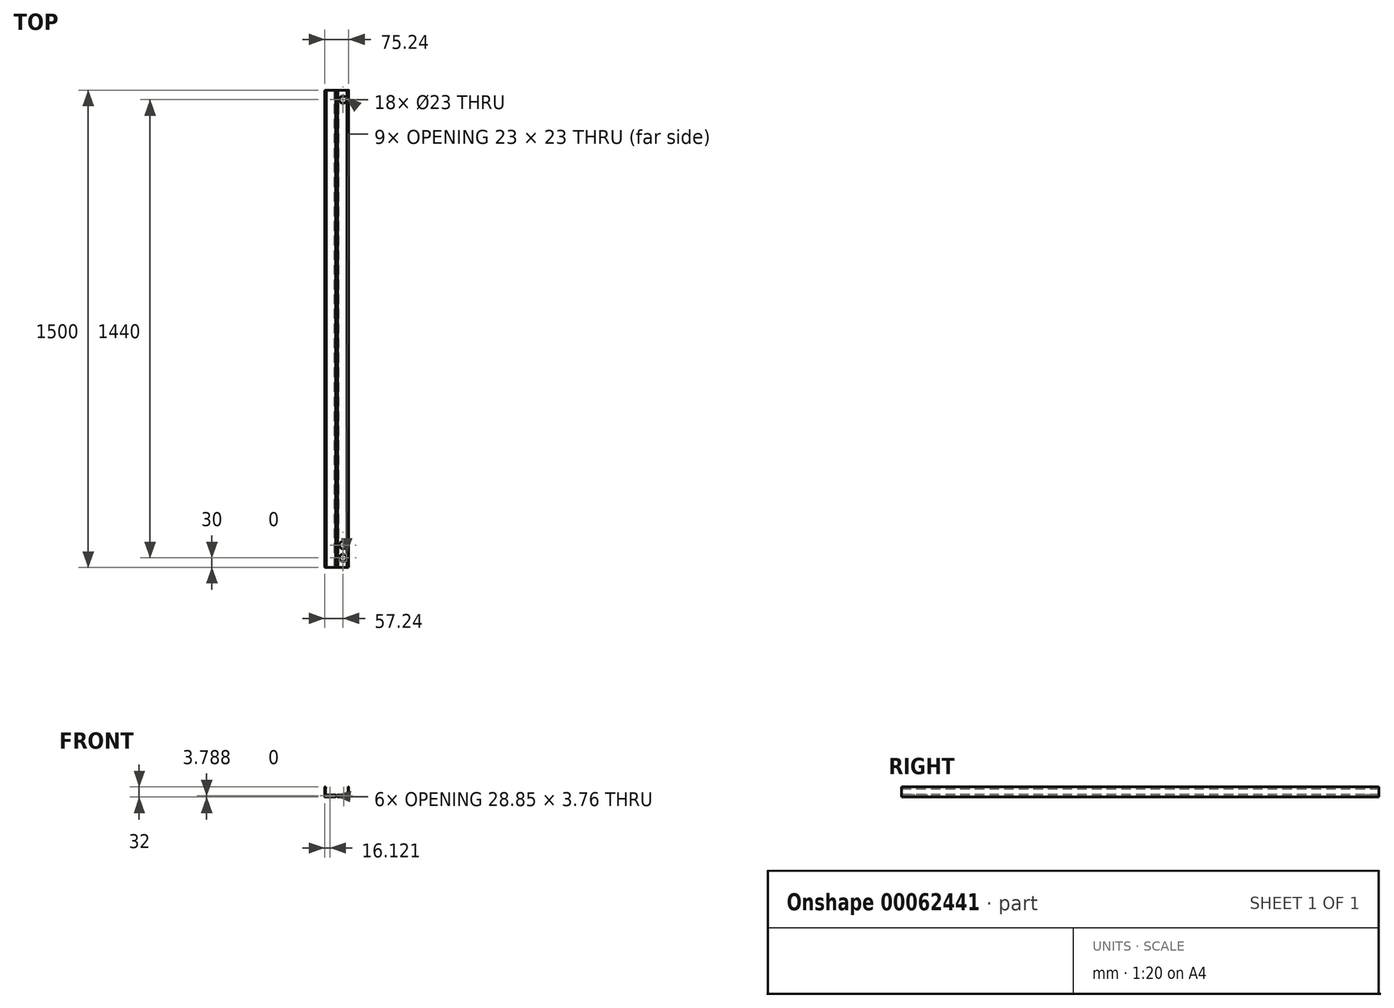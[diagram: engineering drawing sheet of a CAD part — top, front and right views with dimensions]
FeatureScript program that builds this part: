
annotation { "Feature Type Name" : "Feature", "Feature Type Description" : "" }
export const myFeature = defineFeature(function(context is Context, id is Id, definition is map)
    precondition{}
    {
        {
            var Q0;
            Q0=qCreatedBy(makeId("Front.planeOp"),FACE);
            var sketch = newSketch(context, id + "F0", { "sketchPlane" : qUnion([Q0])});
            skLineSegment(sketch, "E0.bottom", {"start": v(0, 0) * mm, "end": v(-34.36, 0) * mm});
            skLineSegment(sketch, "E0.top", {"start": v(0, 32) * mm, "end": v(-2, 32) * mm});
            skLineSegment(sketch, "E0.left", {"start": v(0, 0) * mm, "end": v(0, 32) * mm});
            skLineSegment(sketch, "E0.right", {"start": v(-75.24, 0) * mm, "end": v(-75.24, 32) * mm});
            skLineSegment(sketch, "E1", {"start": v(-73.24, 32) * mm, "end": v(-73.24, 30) * mm});
            skLineSegment(sketch, "E2", {"start": v(-73.24, 30) * mm, "end": v(-71.61, 30) * mm});
            skLineSegment(sketch, "E3", {"start": v(-71.61, 30) * mm, "end": v(-71.5, 28.38) * mm});
            skLineSegment(sketch, "E4", {"start": v(-71.5, 28.38) * mm, "end": v(-73.24, 26.53) * mm});
            skLineSegment(sketch, "E5", {"start": v(-73.24, 26.53) * mm, "end": v(-73.24, 9.03) * mm});
            skLineSegment(sketch, "E6", {"start": v(-73.24, 9.03) * mm, "end": v(-69.92, 7.45) * mm});
            skLineSegment(sketch, "E7", {"start": v(-69.92, 7.45) * mm, "end": v(-41.29, 7.45) * mm});
            skLineSegment(sketch, "E8", {"start": v(-41.29, 7.45) * mm, "end": v(-39.54, 5.37) * mm});
            skLineSegment(sketch, "E9.MirrorCS", {"start": v(-2, 26.4) * mm, "end": v(-2.4, 9.03) * mm});
            skLineSegment(sketch, "E10.MirrorCS", {"start": v(-3.74, 28.26) * mm, "end": v(-2, 26.4) * mm});
            skLineSegment(sketch, "E11.MirrorCS", {"start": v(-2, 32) * mm, "end": v(-2, 30) * mm});
            skLineSegment(sketch, "E12.MirrorCS", {"start": v(-2.4, 9.03) * mm, "end": v(-5.72, 7.45) * mm});
            skLineSegment(sketch, "E13.MirrorCS", {"start": v(-5.72, 7.45) * mm, "end": v(-34.35, 7.45) * mm});
            skLineSegment(sketch, "E14.MirrorCS", {"start": v(-34.35, 7.45) * mm, "end": v(-36.1, 5.37) * mm});
            skLineSegment(sketch, "E15.MirrorCS", {"start": v(-3.63, 30) * mm, "end": v(-3.74, 28.26) * mm});
            skLineSegment(sketch, "E16.MirrorCS", {"start": v(-2, 30) * mm, "end": v(-3.63, 30) * mm});
            skLineSegment(sketch, "E17", {"start": v(-36.1, 5.37) * mm, "end": v(-39.54, 5.37) * mm});
            skLineSegment(sketch, "E18.trimOffspring", {"start": v(-73.24, 32) * mm, "end": v(-75.24, 32) * mm});
            skLineSegment(sketch, "E19", {"start": v(-44.7, 1.91) * mm, "end": v(-73.36, 1.91) * mm});
            skLineSegment(sketch, "E20", {"start": v(-73.36, 1.91) * mm, "end": v(-73.4, 2.5) * mm});
            skLineSegment(sketch, "E21", {"start": v(-73.4, 2.5) * mm, "end": v(-71.75, 2.59) * mm});
            skLineSegment(sketch, "E22", {"start": v(-71.75, 2.59) * mm, "end": v(-71.79, 3.29) * mm});
            skLineSegment(sketch, "E23", {"start": v(-71.79, 3.29) * mm, "end": v(-73.54, 3.64) * mm});
            skLineSegment(sketch, "E24", {"start": v(-73.54, 3.64) * mm, "end": v(-73.2, 5.33) * mm});
            skLineSegment(sketch, "E25", {"start": v(-73.2, 5.33) * mm, "end": v(-71.6, 5.67) * mm});
            skLineSegment(sketch, "E26", {"start": v(-71.6, 5.67) * mm, "end": v(-70.68, 4.5) * mm});
            skLineSegment(sketch, "E27", {"start": v(-70.68, 4.5) * mm, "end": v(-69.94, 5.34) * mm});
            skLineSegment(sketch, "E28", {"start": v(-69.94, 5.34) * mm, "end": v(-44.7, 5.34) * mm});
            skLineSegment(sketch, "E29", {"start": v(-44.7, 5.34) * mm, "end": v(-44.7, 1.91) * mm});
            skLineSegment(sketch, "E30", {"start": v(-37.74, 4.09) * mm, "end": v(-41.06, 4.09) * mm});
            skLineSegment(sketch, "E31", {"start": v(-41.06, 4.09) * mm, "end": v(-42.08, 5.37) * mm});
            skLineSegment(sketch, "E32", {"start": v(-42.08, 5.37) * mm, "end": v(-43.15, 5.34) * mm});
            skLineSegment(sketch, "E33", {"start": v(-43.15, 5.34) * mm, "end": v(-43.04, 1.31) * mm});
            skLineSegment(sketch, "E34", {"start": v(-43.04, 1.31) * mm, "end": v(-41, 1.28) * mm});
            skLineSegment(sketch, "E35", {"start": v(-41, 1.28) * mm, "end": v(-41, 0) * mm});
            skLineSegment(sketch, "E36.trimOffspring", {"start": v(-41, 0) * mm, "end": v(-75.24, 0) * mm});
            skLineSegment(sketch, "E37.MirrorCS", {"start": v(-32.33, 1.31) * mm, "end": v(-34.36, 1.28) * mm});
            skLineSegment(sketch, "E38.MirrorCS", {"start": v(-37.74, 4.09) * mm, "end": v(-34.3, 4.09) * mm});
            skLineSegment(sketch, "E39.MirrorCS", {"start": v(-32.22, 5.34) * mm, "end": v(-32.33, 1.31) * mm});
            skLineSegment(sketch, "E40.MirrorCS", {"start": v(-34.36, 0) * mm, "end": v(-0.12, 0) * mm});
            skLineSegment(sketch, "E41.MirrorCS", {"start": v(-33.29, 5.37) * mm, "end": v(-32.22, 5.34) * mm});
            skLineSegment(sketch, "E42.MirrorCS", {"start": v(-34.36, 1.28) * mm, "end": v(-34.36, 0) * mm});
            skLineSegment(sketch, "E43.MirrorCS", {"start": v(-34.3, 4.09) * mm, "end": v(-33.29, 5.37) * mm});
            skLineSegment(sketch, "E44.MirrorCS", {"start": v(-75.24, 0) * mm, "end": v(-41, 0) * mm});
            skLineSegment(sketch, "E45.MirrorCS", {"start": v(-2.04, 5.33) * mm, "end": v(-3.64, 5.67) * mm});
            skLineSegment(sketch, "E46.MirrorCS", {"start": v(-4.56, 4.5) * mm, "end": v(-5.3, 5.34) * mm});
            skLineSegment(sketch, "E47.MirrorCS", {"start": v(-3.49, 2.59) * mm, "end": v(-3.45, 3.29) * mm});
            skLineSegment(sketch, "E48.MirrorCS", {"start": v(-1.88, 1.91) * mm, "end": v(-1.85, 2.5) * mm});
            skLineSegment(sketch, "E49.MirrorCS", {"start": v(-3.64, 5.67) * mm, "end": v(-4.56, 4.5) * mm});
            skLineSegment(sketch, "E50.MirrorCS", {"start": v(-30.55, 5.34) * mm, "end": v(-30.55, 1.91) * mm});
            skLineSegment(sketch, "E51.MirrorCS", {"start": v(-1.7, 3.64) * mm, "end": v(-2.04, 5.33) * mm});
            skLineSegment(sketch, "E52.MirrorCS", {"start": v(-5.3, 5.34) * mm, "end": v(-30.55, 5.34) * mm});
            skLineSegment(sketch, "E53.MirrorCS", {"start": v(-3.45, 3.29) * mm, "end": v(-1.7, 3.64) * mm});
            skLineSegment(sketch, "E54.MirrorCS", {"start": v(-1.85, 2.5) * mm, "end": v(-3.49, 2.59) * mm});
            skLineSegment(sketch, "E55.MirrorCS", {"start": v(-30.55, 1.91) * mm, "end": v(-1.88, 1.91) * mm});
            skSolve(sketch);
        }
        {
            var Q0;
            Q0=makeQuery(id+"F0.imprint","IMPRINT",FACE,{"disambiguationData":[TD([[makeQuery(id+"F0.imprint","IMPRINT",EDGE,{"derivedFrom":sQuery(id+"F0.wireOp",EDGE,"E0.bottom")}),-1.0]])]});
            extrude(context, id + "F1", {"entities" : qUnion([Q0]), "endBound" : BoundingType.SYMMETRIC, "depth" : 1500 * mm});
        }
        {
            var Q0;
            Q0=makeQuery(id+"F1.opExtrude","SWEPT_EDGE",EDGE,{"disambiguationData":[OSD([sQuery(id+"F0.wireOp",EDGE,"E0.right"),sQuery(id+"F0.wireOp",EDGE,"E18.trimOffspring")])]});
            var Q1;
            Q1=makeQuery(id+"F1.opExtrude","SWEPT_EDGE",EDGE,{"disambiguationData":[OSD([sQuery(id+"F0.wireOp",EDGE,"E0.top"),sQuery(id+"F0.wireOp",EDGE,"E0.left")])]});
            var Q2;
            Q2=makeQuery(id+"F1.opExtrude","SWEPT_EDGE",EDGE,{"disambiguationData":[OSD([sQuery(id+"F0.wireOp",EDGE,"E0.bottom"),sQuery(id+"F0.wireOp",EDGE,"E0.left")])]});
            var Q3;
            Q3=makeQuery(id+"F1.opExtrude","SWEPT_EDGE",EDGE,{"disambiguationData":[OSD([sQuery(id+"F0.wireOp",EDGE,"E0.right"),sQuery(id+"F0.wireOp",EDGE,"E44.MirrorCS")])]});
            var Q4;
            Q4=makeQuery(id+"F1.opExtrude","SWEPT_EDGE",EDGE,{"disambiguationData":[OSD([sQuery(id+"F0.wireOp",EDGE,"E35"),sQuery(id+"F0.wireOp",EDGE,"E44.MirrorCS")])]});
            var Q5;
            Q5=makeQuery(id+"F1.opExtrude","SWEPT_EDGE",EDGE,{"disambiguationData":[OSD([sQuery(id+"F0.wireOp",EDGE,"E40.MirrorCS"),sQuery(id+"F0.wireOp",EDGE,"E42.MirrorCS")])]});
            fillet(context, id + "F2", {"entities" : qUnion([Q0, Q1, Q2, Q3, Q4, Q5]), "radius" : 0.5 * mm, "tangentPropagation" : true, "allowEdgeOverflow" : false});
        }
        {
            var Q0;
            Q0=makeQuery(id+"F1.opExtrude","SWEPT_FACE",FACE,{"disambiguationData":[OSD([sQuery(id+"F0.wireOp",EDGE,"E13.MirrorCS")])]});
            var sketch = newSketch(context, id + "F3", { "sketchPlane" : qUnion([Q0])});
            skCircle(sketch, "E56", {"center": v(-18, -720) * mm, "radius": 11.5 * mm});
            skCircle(sketch, "E57.0.1.0", {"center": v(-18, -680) * mm, "radius": 11.5 * mm});
            skLineSegment(sketch, "E57.direction1", {"start": v(-18, -720) * mm, "end": v(-43.4, -720) * mm, "construction": true});
            skLineSegment(sketch, "E57.direction2", {"start": v(-18, -720) * mm, "end": v(-18, -680) * mm, "construction": true});
            skCircle(sketch, "E58", {"center": v(-18, 720) * mm, "radius": 11.5 * mm});
            skSolve(sketch);
        }
        {
            var Q0;
            Q0 = qSketchRegion(id + "F3", true);
            extrude(context, id + "F4", {"entities" : qUnion([Q0]), "operationType" : NewBodyOperationType.REMOVE, "oppositeDirection" : true, "depth" : 25.4 * mm});
        }
    });
